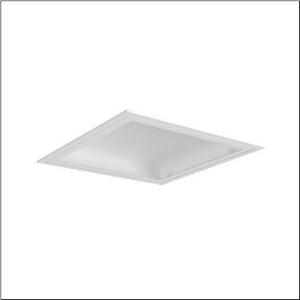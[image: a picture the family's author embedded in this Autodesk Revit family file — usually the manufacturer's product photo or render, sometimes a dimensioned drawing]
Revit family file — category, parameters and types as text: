
# Revit family: mira_21_51fr427a442a
name_source: partatom
category: Lighting Fixtures
units: mm (PartAtom-declared; Revit-internal decimal feet)

## family parameters
Cut with Voids When Loaded = No
Host = Face
Light Source = No
Part Type = Normal
Room Calculation Point = No
Round Connector Dimension = Use Diameter
Shared = No

## types (1)
- Mira 21 (1 x LED, 4860 lm, 37 W, 4000K)
    Apparent Load = 37 VA
    CIE Flux Codes = 50 81 97 100 100
    Color Rendering = 80
    Color Temperature = 4000K
    Default Elevation = 1800 mm
    Description = Mira 21, clean room luminaire, primary light control with reflector, primary optical cover: cover, of PC, light emission: direct distribution, primary light characteristic: symmetric, installation type: recessed, LED, rated luminous flux: 4.860lm, luminous efficacy: 131lm/W, light colour: 840, colour temperature: 4000K, control gear: ON/OFF, with terminal, 3-pole, max. 2.5mm², mains connection: 230V, AC, 50/60Hz, rated input power: 37W, luminaire housing, of sheet steel, coated, pure white (RAL 9010), with concealed spring brackets, module: M625, length: 623mm, width: 623mm, height: 115mm, protection rating (complete): IP54, insulation class (complete): insulation class I (protective earthing), certification: CE, UKCA, permissible operating ambient temperature: -5..+40°C, standard: EN 50419, packaging unit: 1 piece
    Height = 0 mm  [stored 0 ft]
    Lamp = 1 x LED
    Lamp Light Flux = 4860 lm
    Lamp Power = 37 W
    Lamp count = 1
    Length = 625 mm
    Luminous efficacy = 131 lm/W
    Manufacturer = Siteco
    ModVariant = No
    Model = 51FR427A442A
    Mounting Place = Ceiling
    Mounting Type = Recessed
    Number of Poles = 1
    OnlyDefault = Yes
    Power Factor = 1
    Product Name = Mira 21
    Product group = clean room luminaire | ceiling recessed
    ProductGroupID = 402
    Protection Class = Protection class I
    Protection Degree = IP 54
    RLX_Detail_Level = 1
    RLX_Emergency_Light_Flux = 0 lm
    RLX_Emergency_Type = 0
    RLX_Emergency_Type_DB = No
    RlxData = <blob elided: 13381 chars, md5=fbe64520>
    Socket = socket
    Standby Power = 0 W
    System Light Flux = 4860 lm
    System Power = 37 W
    Type Comments = Product without accessories
    Type Image = l_1007109.jpg
    URL = http://relux.com
    VarID = ---
    Voltage = 0 V
    Weight = 0.00 kg
    Width = 625 mm

note: [stored X ft] marks values corroborated as IEEE doubles in the binary element streams (Revit-internal decimal feet)

## geometry (parser evidence)
native form markers: Sweep x9
no freeform markers — native parametric forms only
